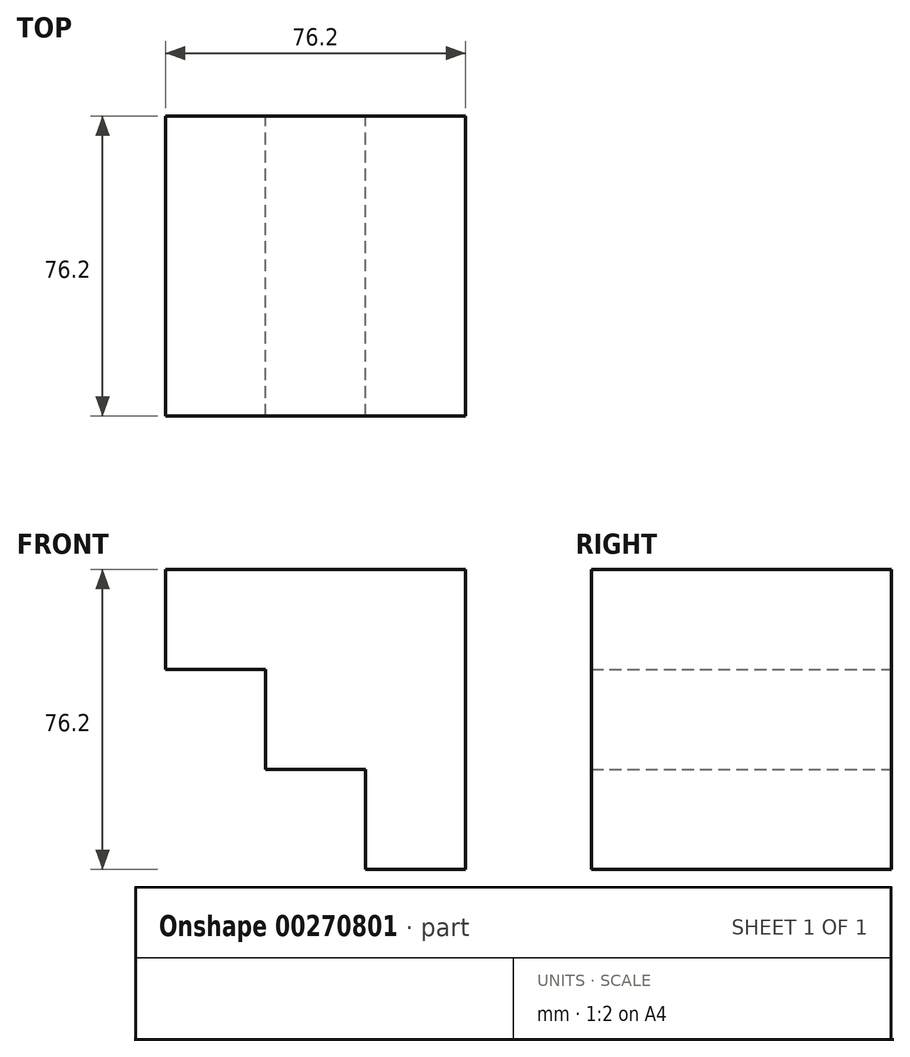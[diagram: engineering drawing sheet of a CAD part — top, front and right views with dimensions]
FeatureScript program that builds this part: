
annotation { "Feature Type Name" : "Feature", "Feature Type Description" : "" }
export const myFeature = defineFeature(function(context is Context, id is Id, definition is map)
    precondition{}
    {
        {
            var Q0;
            Q0=qCreatedBy(makeId("Front.planeOp"),FACE);
            var sketch = newSketch(context, id + "F0", { "sketchPlane" : qUnion([Q0])});
            skLineSegment(sketch, "E0", {"start": v(-63.72, 52.9) * mm, "end": v(12.48, 52.9) * mm});
            skLineSegment(sketch, "E1", {"start": v(12.48, 52.9) * mm, "end": v(12.48, -23.3) * mm});
            skLineSegment(sketch, "E2", {"start": v(12.48, -23.3) * mm, "end": v(-12.92, -23.3) * mm});
            skLineSegment(sketch, "E3", {"start": v(-12.92, -23.3) * mm, "end": v(-12.92, 2.1) * mm});
            skLineSegment(sketch, "E4", {"start": v(-12.92, 2.1) * mm, "end": v(-38.32, 2.1) * mm});
            skLineSegment(sketch, "E5", {"start": v(-38.32, 2.1) * mm, "end": v(-38.32, 27.5) * mm});
            skLineSegment(sketch, "E6", {"start": v(-38.32, 27.5) * mm, "end": v(-63.72, 27.5) * mm});
            skLineSegment(sketch, "E7", {"start": v(-63.72, 27.5) * mm, "end": v(-63.72, 52.9) * mm});
            skSolve(sketch);
        }
        {
            var Q0;
            Q0 = qSketchRegion(id + "F0", true);
            extrude(context, id + "F1", {"entities" : qUnion([Q0]), "depth" : 76.2 * mm});
        }
    });
